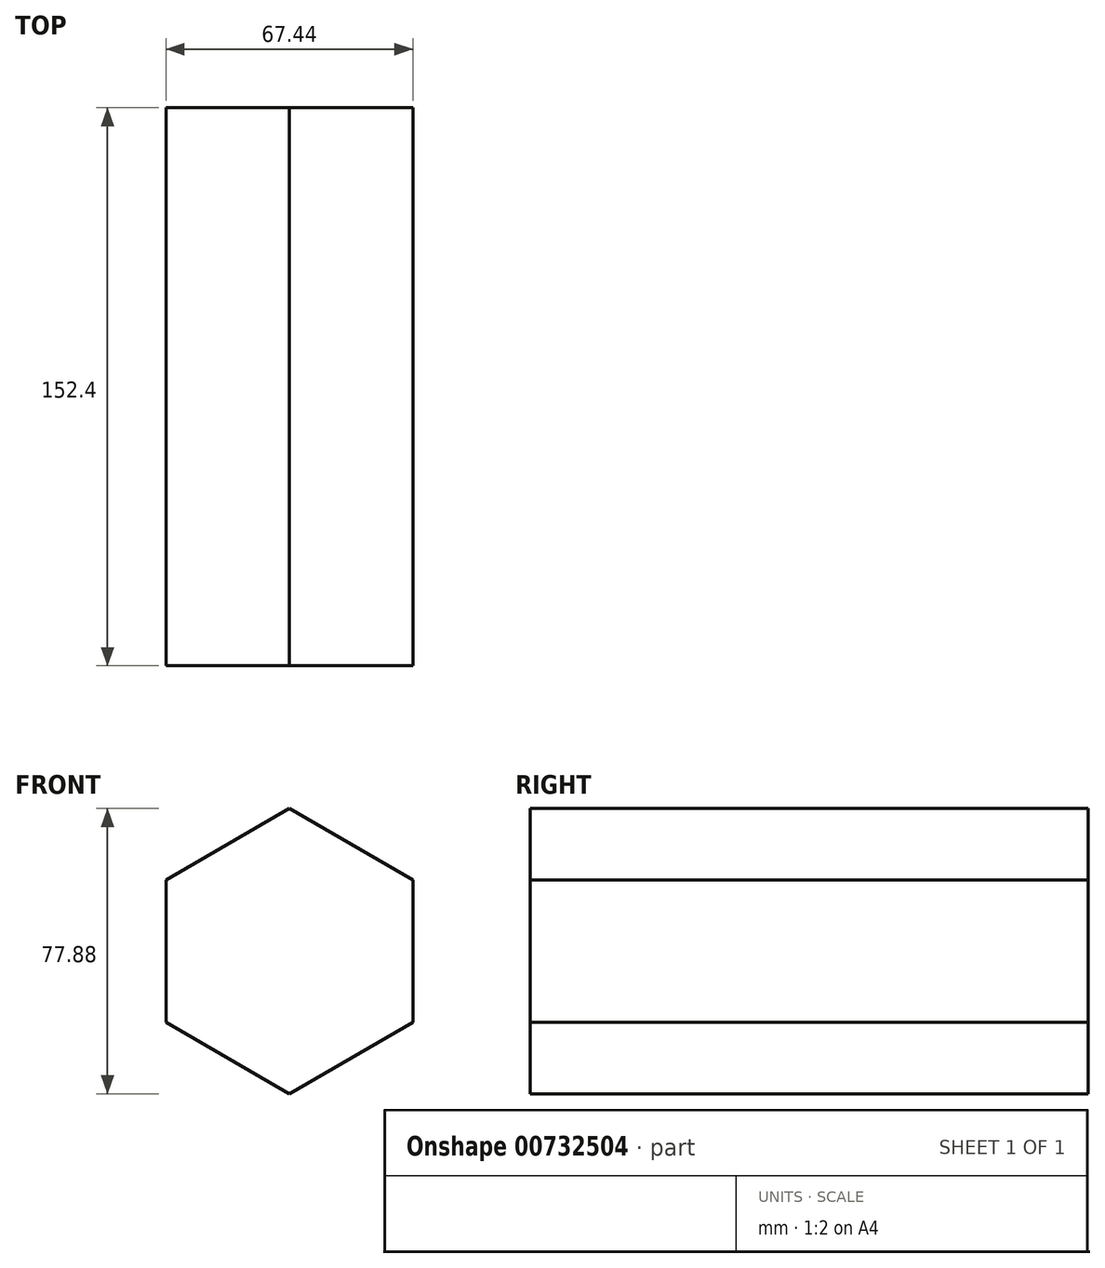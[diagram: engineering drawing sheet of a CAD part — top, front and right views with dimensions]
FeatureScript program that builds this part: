
annotation { "Feature Type Name" : "Feature", "Feature Type Description" : "" }
export const myFeature = defineFeature(function(context is Context, id is Id, definition is map)
    precondition{}
    {
        {
            var Q0;
            Q0=qCreatedBy(makeId("Front.planeOp"),FACE);
            var sketch = newSketch(context, id + "F0", { "sketchPlane" : qUnion([Q0])});
            skCircle(sketch, "E0.cCircle", {"center": v(0, 0) * mm, "radius": 33.72 * mm, "construction": true});
            skLineSegment(sketch, "E0.0", {"start": v(-33.72, -19.47) * mm, "end": v(-33.72, 19.47) * mm});
            skLineSegment(sketch, "E0.1", {"start": v(-33.72, 19.47) * mm, "end": v(0, 38.94) * mm});
            skLineSegment(sketch, "E0.2", {"start": v(0, 38.94) * mm, "end": v(33.72, 19.47) * mm});
            skLineSegment(sketch, "E0.3", {"start": v(33.72, 19.47) * mm, "end": v(33.72, -19.47) * mm});
            skLineSegment(sketch, "E0.4", {"start": v(33.72, -19.47) * mm, "end": v(0, -38.94) * mm});
            skLineSegment(sketch, "E0.5", {"start": v(0, -38.94) * mm, "end": v(-33.72, -19.47) * mm});
            skPoint(sketch, "E0.0.midPoint", {"position": v(-33.72, 0) * mm});
            skSolve(sketch);
        }
        {
            var Q0;
            Q0=makeQuery(id+"F0.imprint","IMPRINT",FACE,{"disambiguationData":[TD([[makeQuery(id+"F0.imprint","IMPRINT",EDGE,{"derivedFrom":sQuery(id+"F0.wireOp",EDGE,"E0.0")}),-1.0]])]});
            extrude(context, id + "F1", {"entities" : qUnion([Q0]), "depth" : 25.4 * mm, "offsetDistance" : 25.4 * mm});
        }
        {
            var Q0;
            Q0=makeQuery(id+"F1.opExtrude","CAP_FACE",FACE,{"disambiguationData":[OSD([sQuery(id+"F0.wireOp",EDGE,"E0.0"),sQuery(id+"F0.wireOp",EDGE,"E0.1"),sQuery(id+"F0.wireOp",EDGE,"E0.2"),sQuery(id+"F0.wireOp",EDGE,"E0.3"),sQuery(id+"F0.wireOp",EDGE,"E0.4"),sQuery(id+"F0.wireOp",EDGE,"E0.5")])],"isStart":false});
            extrude(context, id + "F2", {"entities" : qUnion([Q0]), "operationType" : NewBodyOperationType.ADD, "depth" : 127 * mm, "offsetDistance" : 25.4 * mm});
        }
    });
